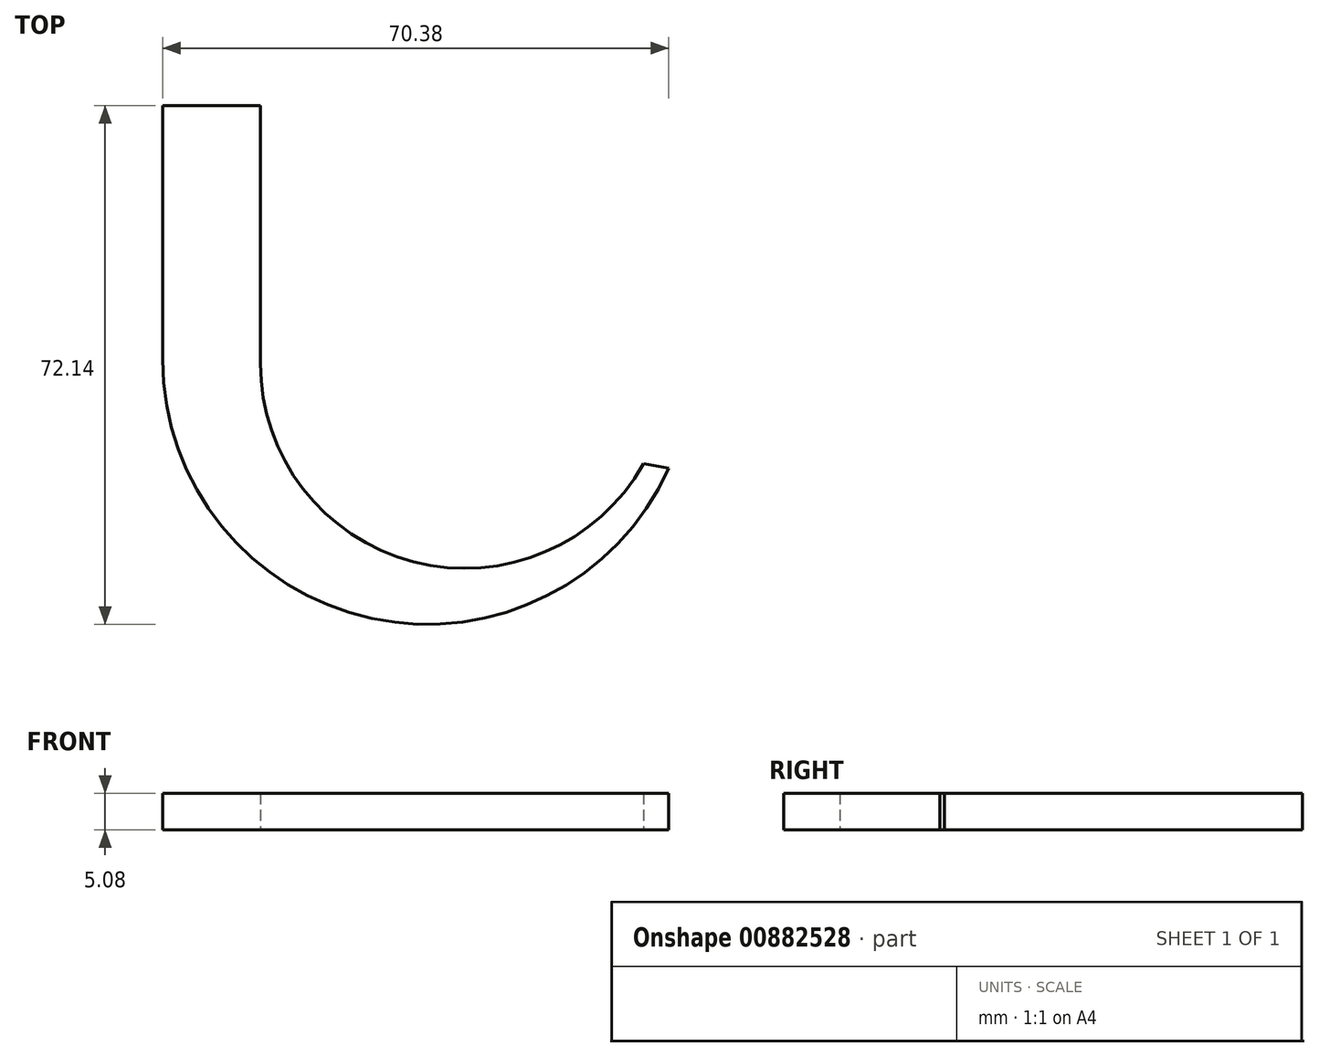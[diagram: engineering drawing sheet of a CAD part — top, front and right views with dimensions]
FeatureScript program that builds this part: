
annotation { "Feature Type Name" : "Feature", "Feature Type Description" : "" }
export const myFeature = defineFeature(function(context is Context, id is Id, definition is map)
    precondition{}
    {
        {
            var Q0;
            Q0=qCreatedBy(makeId("Top.planeOp"),FACE);
            var sketch = newSketch(context, id + "F0", { "sketchPlane" : qUnion([Q0])});
            skLineSegment(sketch, "E0", {"start": v(-35.3, 44.53) * mm, "end": v(-35.3, 27.3) * mm});
            skLineSegment(sketch, "E1", {"start": v(-35.3, 44.53) * mm, "end": v(-21.72, 44.53) * mm});
            skLineSegment(sketch, "E2", {"start": v(-21.72, 44.53) * mm, "end": v(-21.72, 8.62) * mm});
            skLineSegment(sketch, "E3", {"start": v(-35.3, 27.3) * mm, "end": v(-35.3, 9.2) * mm});
            skArc(sketch, "E4", {"start": v(-35.3, 9.2) * mm, "mid": v(-6.2, -26.8) * mm, "end": v(35.08, -5.9) * mm});
            skArc(sketch, "E5", {"start": v(-21.72, 8.62) * mm, "mid": v(-0.45, -18.9) * mm, "end": v(31.55, -5.28) * mm});
            skLineSegment(sketch, "E6", {"start": v(31.55, -5.28) * mm, "end": v(35.08, -5.9) * mm});
            skSolve(sketch);
        }
        {
            var Q0;
            Q0 = qSketchRegion(id + "F0", true);
            extrude(context, id + "F1", {"entities" : qUnion([Q0]), "depth" : 5.08 * mm, "offsetDistance" : 25.4 * mm});
        }
    });
